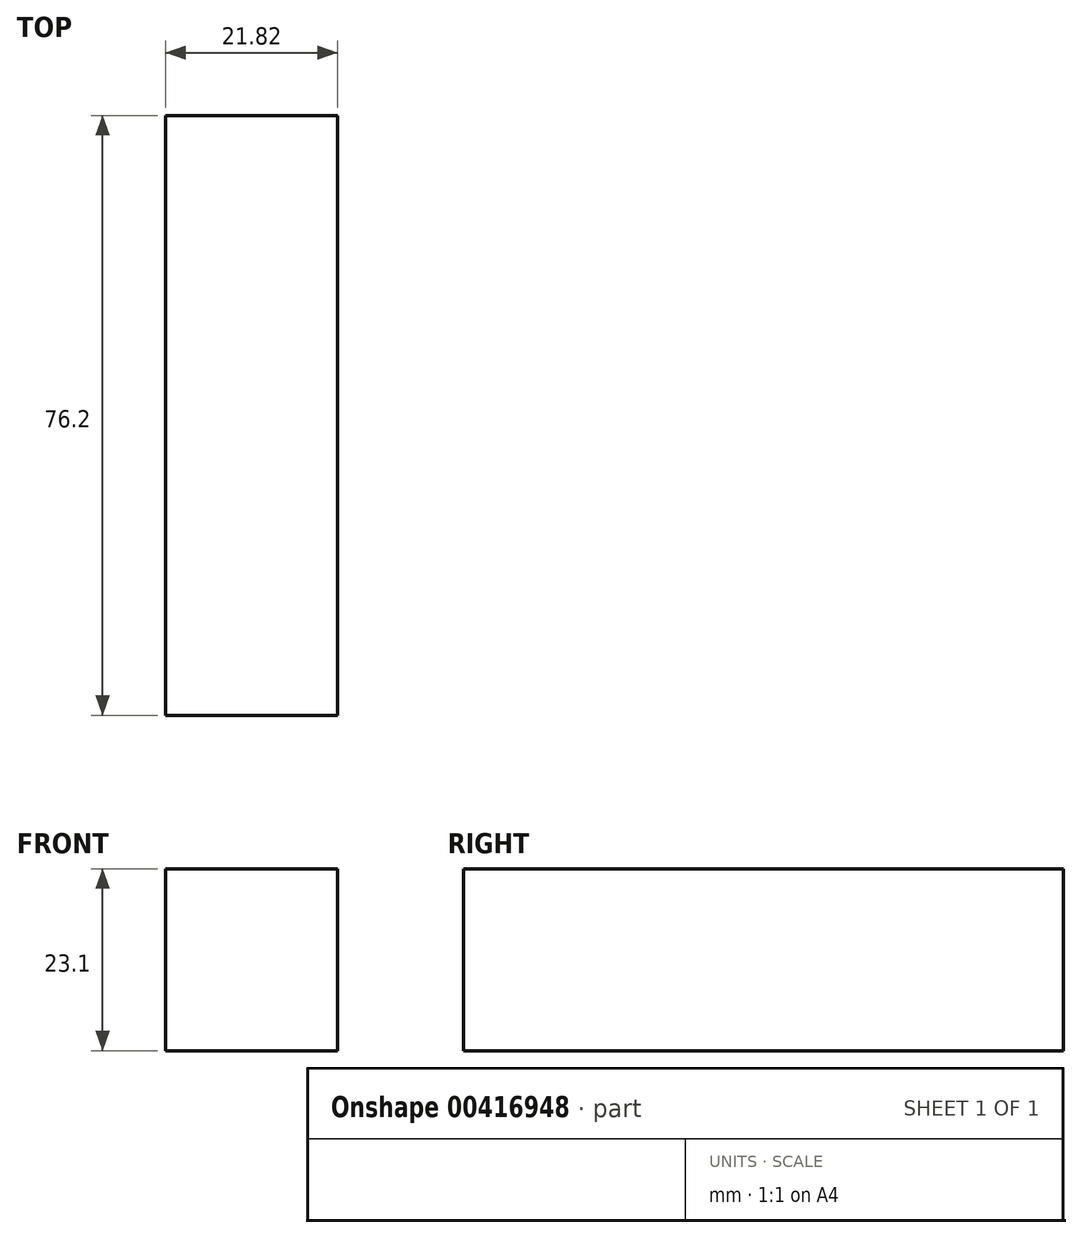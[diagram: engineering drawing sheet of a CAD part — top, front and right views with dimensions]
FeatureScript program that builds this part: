
annotation { "Feature Type Name" : "Feature", "Feature Type Description" : "" }
export const myFeature = defineFeature(function(context is Context, id is Id, definition is map)
    precondition{}
    {
        {
            var Q0;
            Q0=qCreatedBy(makeId("Front.planeOp"),FACE);
            var sketch = newSketch(context, id + "F0", { "sketchPlane" : qUnion([Q0])});
            skLineSegment(sketch, "E0.bottom", {"start": v(-21.82, 23.1) * mm, "end": v(0, 23.1) * mm});
            skLineSegment(sketch, "E0.top", {"start": v(-21.82, 0) * mm, "end": v(0, 0) * mm});
            skLineSegment(sketch, "E0.left", {"start": v(-21.82, 23.1) * mm, "end": v(-21.82, 0) * mm});
            skLineSegment(sketch, "E0.right", {"start": v(0, 23.1) * mm, "end": v(0, 0) * mm});
            skSolve(sketch);
        }
        {
            var Q0;
            Q0=makeQuery(id+"F0.imprint","IMPRINT",FACE,{"disambiguationData":[TD([[makeQuery(id+"F0.imprint","IMPRINT",EDGE,{"derivedFrom":sQuery(id+"F0.wireOp",EDGE,"E0.bottom")}),-1.0]])]});
            extrude(context, id + "F1", {"entities" : qUnion([Q0]), "depth" : 76.2 * mm, "offsetDistance" : 25.4 * mm});
        }
    });
